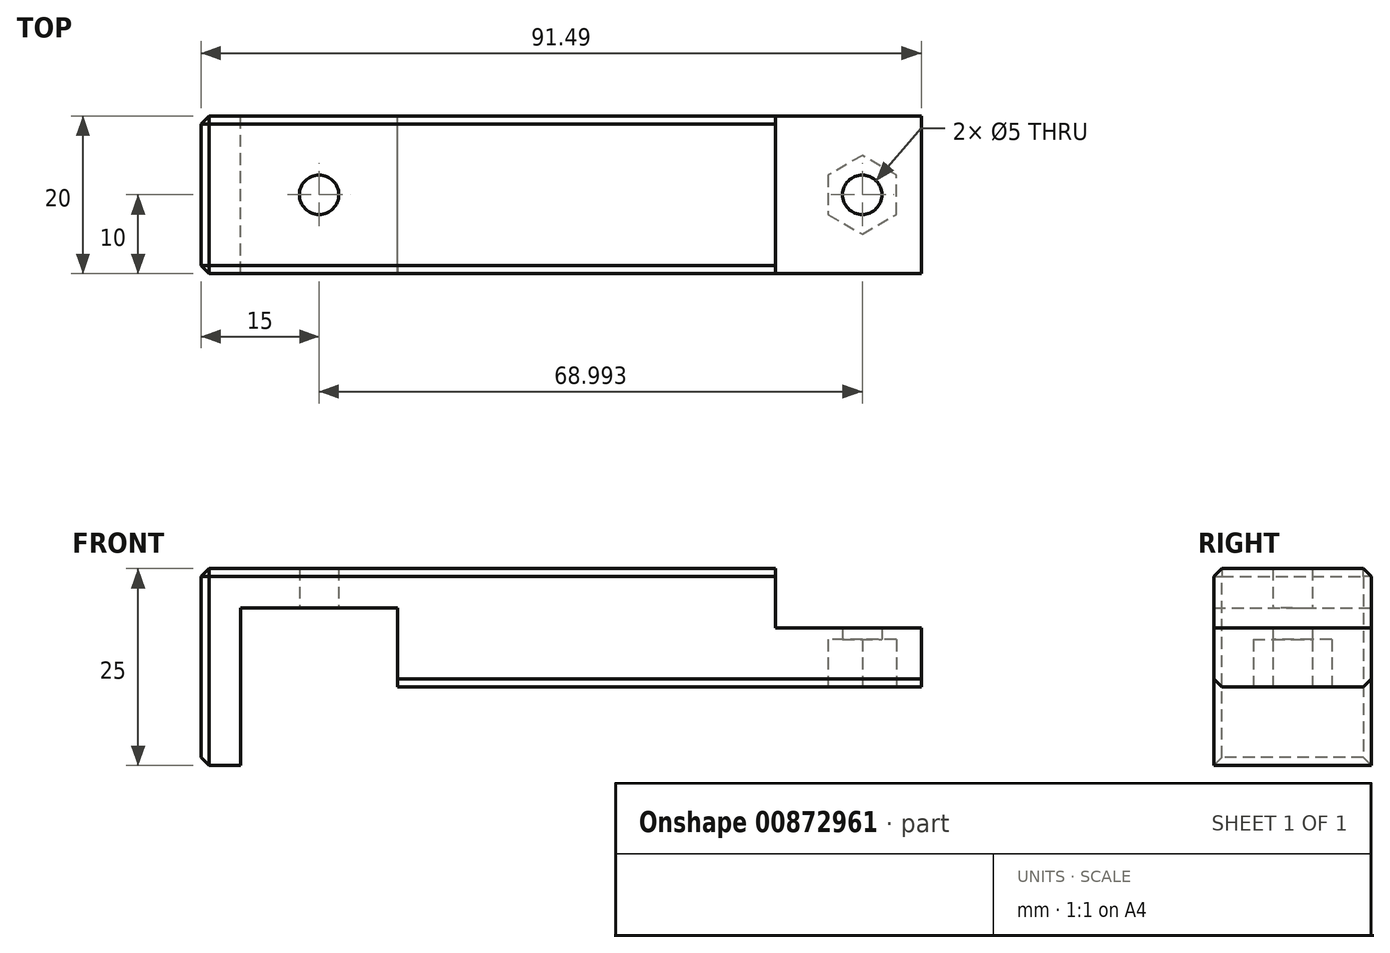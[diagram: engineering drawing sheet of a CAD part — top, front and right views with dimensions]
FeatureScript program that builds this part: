
annotation { "Feature Type Name" : "Feature", "Feature Type Description" : "" }
export const myFeature = defineFeature(function(context is Context, id is Id, definition is map)
    precondition{}
    {
        {
            var Q0;
            Q0=qCreatedBy(makeId("Front.planeOp"),FACE);
            var sketch = newSketch(context, id + "F0", { "sketchPlane" : qUnion([Q0])});
            skLineSegment(sketch, "E0", {"start": v(-44.53, -17.5) * mm, "end": v(-44.53, 7.5) * mm});
            skLineSegment(sketch, "E1", {"start": v(-44.53, 7.5) * mm, "end": v(0, 7.5) * mm});
            skLineSegment(sketch, "E2", {"start": v(0, -7.5) * mm, "end": v(46.96, -7.5) * mm});
            skLineSegment(sketch, "E3", {"start": v(46.96, -7.5) * mm, "end": v(46.96, 0) * mm});
            skLineSegment(sketch, "E4", {"start": v(46.96, 0) * mm, "end": v(28.47, 0) * mm});
            skLineSegment(sketch, "E5", {"start": v(28.47, 0) * mm, "end": v(28.47, 7.5) * mm});
            skLineSegment(sketch, "E6", {"start": v(28.47, 7.5) * mm, "end": v(0, 7.5) * mm});
            skLineSegment(sketch, "E7", {"start": v(-44.53, -17.5) * mm, "end": v(-39.53, -17.5) * mm});
            skLineSegment(sketch, "E8", {"start": v(-39.53, -17.5) * mm, "end": v(-39.53, 2.5) * mm});
            skLineSegment(sketch, "E9", {"start": v(-39.53, 2.5) * mm, "end": v(-19.53, 2.5) * mm});
            skLineSegment(sketch, "E10", {"start": v(-19.53, 2.5) * mm, "end": v(-19.53, -7.5) * mm});
            skLineSegment(sketch, "E11", {"start": v(-19.53, -7.5) * mm, "end": v(0, -7.5) * mm});
            skSolve(sketch);
        }
        {
            var Q0;
            Q0=makeQuery(id+"F0.imprint","IMPRINT",FACE,{"disambiguationData":[TD([[makeQuery(id+"F0.imprint","IMPRINT",EDGE,{"derivedFrom":sQuery(id+"F0.wireOp",EDGE,"E0")}),-1.0]])]});
            extrude(context, id + "F1", {"entities" : qUnion([Q0]), "depth" : 20 * mm, "offsetDistance" : 25 * mm});
        }
        {
            var Q0;
            Q0=makeQuery(id+"F1.opExtrude","CAP_EDGE",EDGE,{"disambiguationData":[OSD([sQuery(id+"F0.wireOp",EDGE,"E1"),sQuery(id+"F0.wireOp",EDGE,"E6")])],"isStart":false});
            var Q1;
            Q1=makeQuery(id+"F1.opExtrude","CAP_EDGE",EDGE,{"disambiguationData":[OSD([sQuery(id+"F0.wireOp",EDGE,"E1"),sQuery(id+"F0.wireOp",EDGE,"E6")])],"isStart":true});
            var Q2;
            Q2=makeQuery(id+"F1.opExtrude","SWEPT_EDGE",EDGE,{"disambiguationData":[OSD([sQuery(id+"F0.wireOp",EDGE,"E0"),sQuery(id+"F0.wireOp",EDGE,"E1")])]});
            var Q3;
            Q3=makeQuery(id+"F1.opExtrude","CAP_EDGE",EDGE,{"disambiguationData":[OSD([sQuery(id+"F0.wireOp",EDGE,"E0")])],"isStart":false});
            var Q4;
            Q4=makeQuery(id+"F1.opExtrude","CAP_EDGE",EDGE,{"disambiguationData":[OSD([sQuery(id+"F0.wireOp",EDGE,"E0")])],"isStart":true});
            var Q5;
            Q5=makeQuery(id+"F1.opExtrude","SWEPT_EDGE",EDGE,{"disambiguationData":[OSD([sQuery(id+"F0.wireOp",EDGE,"E0"),sQuery(id+"F0.wireOp",EDGE,"E7")])]});
            var Q6;
            Q6=makeQuery(id+"F1.opExtrude","CAP_EDGE",EDGE,{"disambiguationData":[OSD([sQuery(id+"F0.wireOp",EDGE,"E2"),sQuery(id+"F0.wireOp",EDGE,"E11")])],"isStart":true});
            var Q7;
            Q7=makeQuery(id+"F1.opExtrude","CAP_EDGE",EDGE,{"disambiguationData":[OSD([sQuery(id+"F0.wireOp",EDGE,"E2"),sQuery(id+"F0.wireOp",EDGE,"E11")])],"isStart":false});
            chamfer(context, id + "F2", {"entities" : qUnion([Q0, Q1, Q2, Q3, Q4, Q5, Q6, Q7]), "width" : 1 * mm, "tangentPropagation" : true});
        }
        {
            var Q0;
            Q0=makeQuery(id+"F1.opExtrude","SWEPT_FACE",FACE,{"disambiguationData":[OSD([sQuery(id+"F0.wireOp",EDGE,"E2"),sQuery(id+"F0.wireOp",EDGE,"E11")])]});
            var sketch = newSketch(context, id + "F3", { "sketchPlane" : qUnion([Q0])});
            skCircle(sketch, "E12", {"center": v(39.46, 10) * mm, "radius": 2.5 * mm});
            skCircle(sketch, "E13", {"center": v(-29.53, 10) * mm, "radius": 2.5 * mm});
            skSolve(sketch);
        }
        {
            var Q0;
            Q0=makeQuery(id+"F3.imprint","IMPRINT",FACE,{"disambiguationData":[TD([[makeQuery(id+"F3.imprint","IMPRINT",EDGE,{"derivedFrom":sQuery(id+"F3.wireOp",EDGE,"E13")}),1.0]])]});
            var Q1;
            Q1=makeQuery(id+"F3.imprint","IMPRINT",FACE,{"disambiguationData":[TD([[makeQuery(id+"F3.imprint","IMPRINT",EDGE,{"derivedFrom":sQuery(id+"F3.wireOp",EDGE,"E12")}),1.0]])]});
            extrude(context, id + "F4", {"entities" : qUnion([Q0, Q1]), "operationType" : NewBodyOperationType.REMOVE, "oppositeDirection" : true, "depth" : 25 * mm, "offsetDistance" : 25 * mm});
        }
        {
            var Q0;
            Q0=makeQuery(id+"F1.opExtrude","SWEPT_FACE",FACE,{"disambiguationData":[OSD([sQuery(id+"F0.wireOp",EDGE,"E2"),sQuery(id+"F0.wireOp",EDGE,"E11")])]});
            var sketch = newSketch(context, id + "F5", { "sketchPlane" : qUnion([Q0])});
            skCircle(sketch, "E14.cCircle", {"center": v(39.46, 10) * mm, "radius": 4.33 * mm, "construction": true});
            skLineSegment(sketch, "E14.0", {"start": v(35.13, 7.5) * mm, "end": v(35.13, 12.5) * mm});
            skLineSegment(sketch, "E14.1", {"start": v(35.13, 12.5) * mm, "end": v(39.46, 15) * mm});
            skLineSegment(sketch, "E14.2", {"start": v(39.46, 15) * mm, "end": v(43.8, 12.5) * mm});
            skLineSegment(sketch, "E14.3", {"start": v(43.8, 12.5) * mm, "end": v(43.8, 7.5) * mm});
            skLineSegment(sketch, "E14.4", {"start": v(43.8, 7.5) * mm, "end": v(39.46, 5) * mm});
            skLineSegment(sketch, "E14.5", {"start": v(39.46, 5) * mm, "end": v(35.13, 7.5) * mm});
            skPoint(sketch, "E14.0.midPoint", {"position": v(35.13, 10) * mm});
            skSolve(sketch);
        }
        {
            var Q0;
            Q0 = qSketchRegion(id + "F5", true);
            extrude(context, id + "F6", {"entities" : qUnion([Q0]), "operationType" : NewBodyOperationType.REMOVE, "oppositeDirection" : true, "depth" : 6 * mm, "offsetDistance" : 25 * mm});
        }
    });
